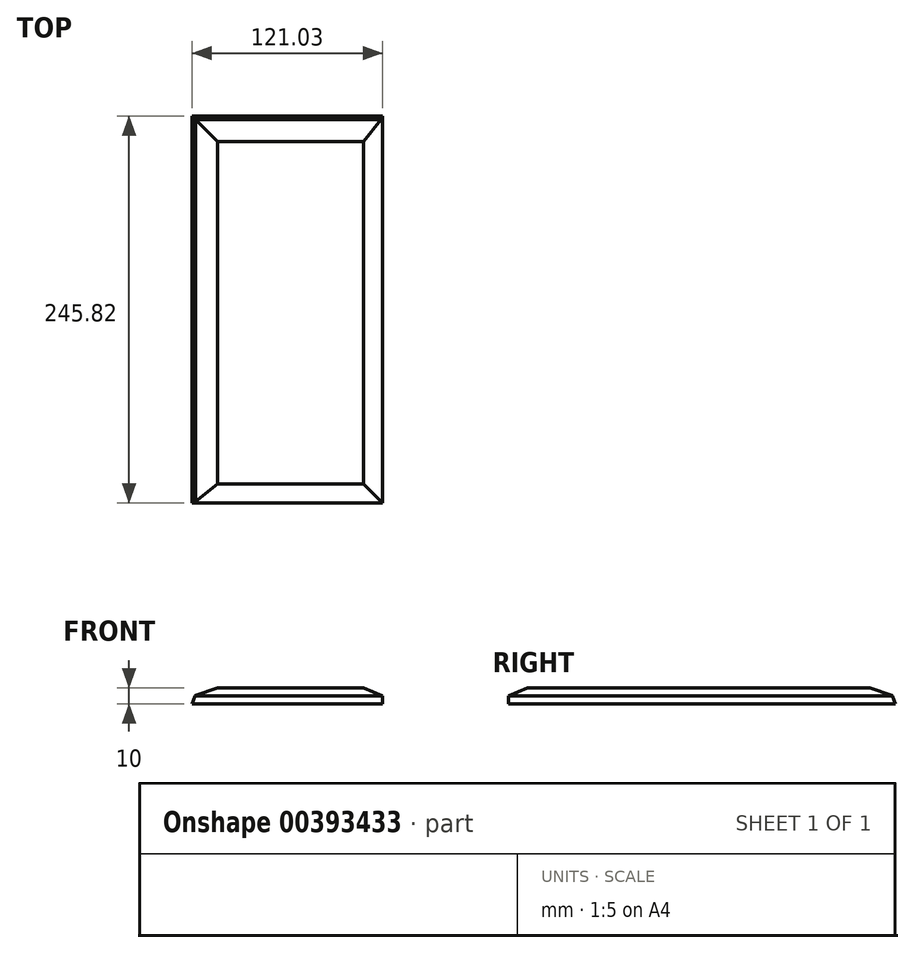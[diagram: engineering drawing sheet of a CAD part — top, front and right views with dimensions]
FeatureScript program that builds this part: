
annotation { "Feature Type Name" : "Feature", "Feature Type Description" : "" }
export const myFeature = defineFeature(function(context is Context, id is Id, definition is map)
    precondition{}
    {
        {
            var Q0;
            Q0=qCreatedBy(makeId("Top.planeOp"),FACE);
            var sketch = newSketch(context, id + "F0", { "sketchPlane" : qUnion([Q0])});
            skLineSegment(sketch, "E0.bottom", {"start": v(-36.58, -32.89) * mm, "end": v(85.28, -32.89) * mm});
            skLineSegment(sketch, "E0.top", {"start": v(-36.58, 213.76) * mm, "end": v(85.28, 213.76) * mm});
            skLineSegment(sketch, "E0.left", {"start": v(-36.58, -32.89) * mm, "end": v(-36.58, 213.76) * mm});
            skLineSegment(sketch, "E0.right", {"start": v(85.28, -32.89) * mm, "end": v(85.28, 213.76) * mm});
            skSolve(sketch);
        }
        {
            var Q0;
            Q0=makeQuery(id+"F0.imprint","IMPRINT",FACE,{"disambiguationData":[TD([[makeQuery(id+"F0.imprint","IMPRINT",EDGE,{"derivedFrom":sQuery(id+"F0.wireOp",EDGE,"E0.bottom")}),1.0]])]});
            extrude(context, id + "F1", {"entities" : qUnion([Q0]), "depth" : 10 * mm});
        }
        {
            var Q0;
            Q0=makeQuery(id+"F1.opExtrude","CAP_EDGE",EDGE,{"disambiguationData":[OSD([sQuery(id+"F0.wireOp",EDGE,"E0.right")])],"isStart":false});
            chamfer(context, id + "F2", {"entities" : qUnion([Q0]), "chamferType" : ChamferType.TWO_OFFSETS, "width1" : 12 * mm, "oppositeDirection" : false, "width2" : 5 * mm, "tangentPropagation" : true});
        }
        {
            var Q0;
            Q0=makeQuery(id+"F1.opExtrude","CAP_EDGE",EDGE,{"disambiguationData":[OSD([sQuery(id+"F0.wireOp",EDGE,"E0.bottom")])],"isStart":false});
            chamfer(context, id + "F3", {"entities" : qUnion([Q0]), "chamferType" : ChamferType.TWO_OFFSETS, "width1" : 12 * mm, "oppositeDirection" : false, "width2" : 5 * mm, "tangentPropagation" : true});
        }
        {
            var Q0;
            Q0=makeQuery(id+"F1.opExtrude","CAP_EDGE",EDGE,{"disambiguationData":[OSD([sQuery(id+"F0.wireOp",EDGE,"E0.top")])],"isStart":false});
            chamfer(context, id + "F4", {"entities" : qUnion([Q0]), "chamferType" : ChamferType.TWO_OFFSETS, "width1" : 12 * mm, "oppositeDirection" : false, "width2" : 5 * mm, "tangentPropagation" : true});
        }
        {
            var Q0;
            Q0=makeQuery(id+"F1.opExtrude","CAP_EDGE",EDGE,{"disambiguationData":[OSD([sQuery(id+"F0.wireOp",EDGE,"E0.left")])],"isStart":false});
            chamfer(context, id + "F5", {"entities" : qUnion([Q0]), "chamferType" : ChamferType.TWO_OFFSETS, "width1" : 12 * mm, "oppositeDirection" : false, "width2" : 5 * mm, "tangentPropagation" : true});
        }
        {
            var Q0;
            {var subQ0=sQuery(id+"F0.wireOp",EDGE,"E0.left");Q0=makeQuery(id+"F5.opChamfer","BLEND_EDGE",EDGE,{"blendedFrom":[makeQuery(id+"F1.opExtrude","CAP_EDGE",EDGE,{"disambiguationData":[OSD([subQ0])],"isStart":false}),makeQuery(id+"F1.opExtrude","CAP_FACE",FACE,{"disambiguationData":[OSD([sQuery(id+"F0.wireOp",EDGE,"E0.bottom"),sQuery(id+"F0.wireOp",EDGE,"E0.top"),subQ0,sQuery(id+"F0.wireOp",EDGE,"E0.right")])],"isStart":false})],"blendedInto":[makeQuery(id+"F1.opExtrude","CAP_FACE",FACE,{"disambiguationData":[OSD([sQuery(id+"F0.wireOp",EDGE,"E0.bottom"),sQuery(id+"F0.wireOp",EDGE,"E0.top"),subQ0,sQuery(id+"F0.wireOp",EDGE,"E0.right")])],"isStart":false})]});}
            chamfer(context, id + "F6", {"entities" : qUnion([Q0]), "chamferType" : ChamferType.TWO_OFFSETS, "width1" : 12 * mm, "oppositeDirection" : false, "width2" : 5 * mm, "tangentPropagation" : true});
        }
        {
            var Q0;
            {var subQ0=sQuery(id+"F0.wireOp",EDGE,"E0.top");Q0=makeQuery(id+"F4.opChamfer","BLEND_EDGE",EDGE,{"blendedFrom":[makeQuery(id+"F1.opExtrude","CAP_EDGE",EDGE,{"disambiguationData":[OSD([subQ0])],"isStart":false}),makeQuery(id+"F1.opExtrude","CAP_FACE",FACE,{"disambiguationData":[OSD([sQuery(id+"F0.wireOp",EDGE,"E0.bottom"),subQ0,sQuery(id+"F0.wireOp",EDGE,"E0.left"),sQuery(id+"F0.wireOp",EDGE,"E0.right")])],"isStart":false})],"blendedInto":[makeQuery(id+"F1.opExtrude","CAP_FACE",FACE,{"disambiguationData":[OSD([sQuery(id+"F0.wireOp",EDGE,"E0.bottom"),subQ0,sQuery(id+"F0.wireOp",EDGE,"E0.left"),sQuery(id+"F0.wireOp",EDGE,"E0.right")])],"isStart":false})]});}
            chamfer(context, id + "F7", {"entities" : qUnion([Q0]), "chamferType" : ChamferType.TWO_OFFSETS, "width1" : 12 * mm, "oppositeDirection" : false, "width2" : 5 * mm, "tangentPropagation" : true});
        }
    });
